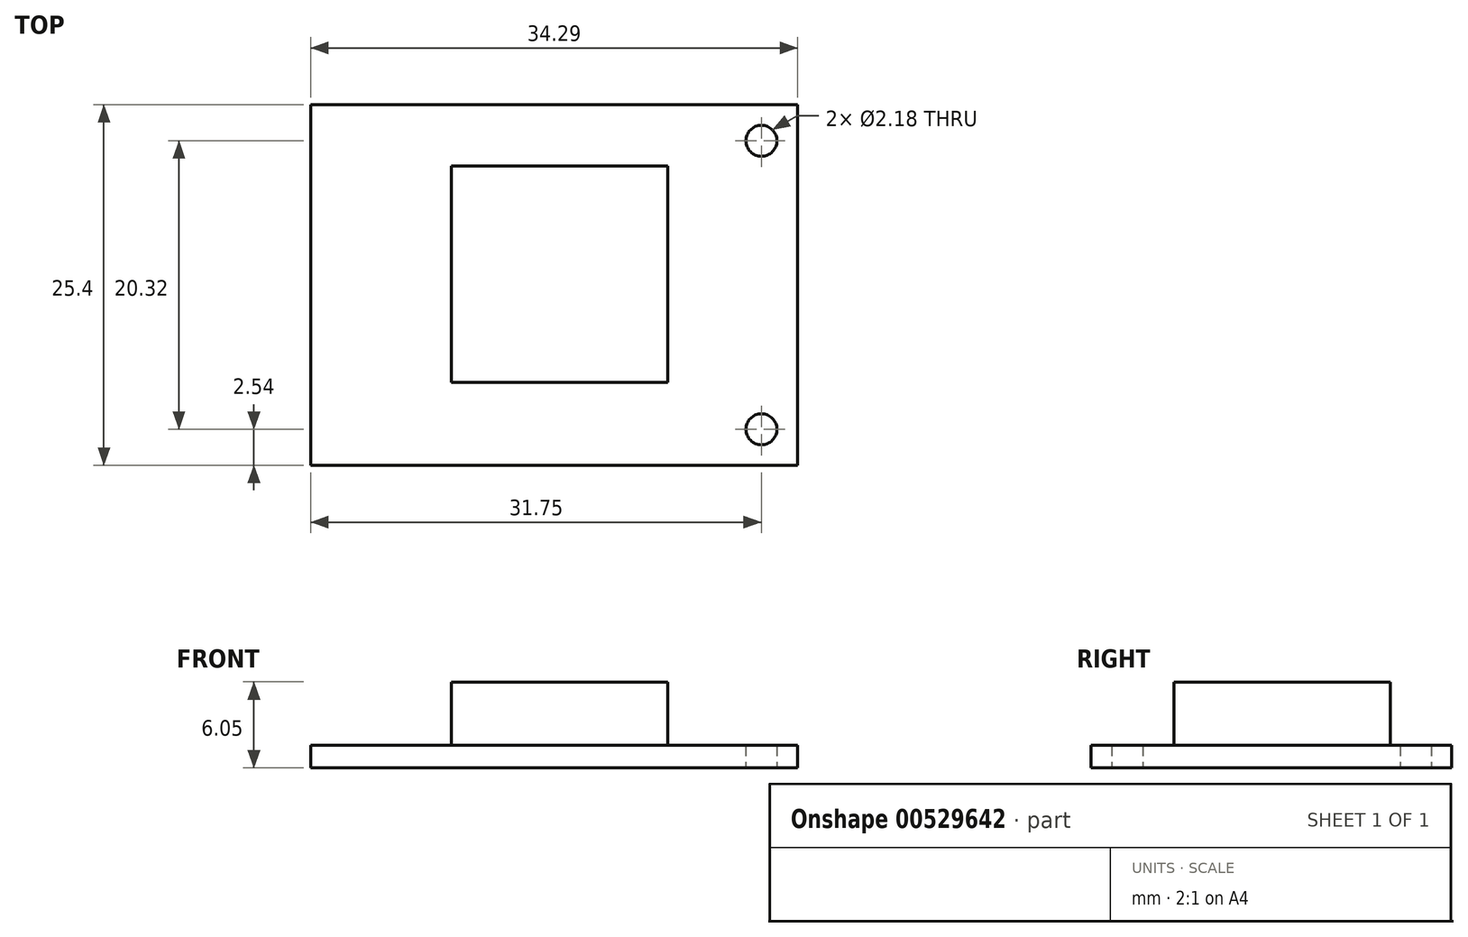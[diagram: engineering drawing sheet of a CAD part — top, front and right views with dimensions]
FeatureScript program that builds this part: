
annotation { "Feature Type Name" : "Feature", "Feature Type Description" : "" }
export const myFeature = defineFeature(function(context is Context, id is Id, definition is map)
    precondition{}
    {
        {
            var Q0;
            Q0=qCreatedBy(makeId("Top.planeOp"),FACE);
            var sketch = newSketch(context, id + "F0", { "sketchPlane" : qUnion([Q0])});
            skLineSegment(sketch, "E0.bottom", {"start": v(0, 0) * mm, "end": v(34.3, 0) * mm});
            skLineSegment(sketch, "E0.top", {"start": v(0, 25.4) * mm, "end": v(34.3, 25.4) * mm});
            skLineSegment(sketch, "E0.left", {"start": v(0, 0) * mm, "end": v(0, 25.4) * mm});
            skLineSegment(sketch, "E0.right", {"start": v(34.3, 0) * mm, "end": v(34.3, 25.4) * mm});
            skCircle(sketch, "E1", {"center": v(31.75, 22.86) * mm, "radius": 1.1 * mm});
            skCircle(sketch, "E2", {"center": v(31.75, 2.54) * mm, "radius": 1.1 * mm});
            skLineSegment(sketch, "E3.bottom", {"start": v(9.9, 21.08) * mm, "end": v(25.15, 21.08) * mm});
            skLineSegment(sketch, "E3.top", {"start": v(9.9, 5.84) * mm, "end": v(25.15, 5.84) * mm});
            skLineSegment(sketch, "E3.left", {"start": v(9.9, 21.08) * mm, "end": v(9.9, 5.84) * mm});
            skLineSegment(sketch, "E3.right", {"start": v(25.15, 21.08) * mm, "end": v(25.15, 5.84) * mm});
            skSolve(sketch);
        }
        {
            var Q0;
            Q0=makeQuery(id+"F0.imprint","IMPRINT",FACE,{"disambiguationData":[TD([[makeQuery(id+"F0.imprint","IMPRINT",EDGE,{"derivedFrom":sQuery(id+"F0.wireOp",EDGE,"E3.bottom")}),-1.0]])]});
            extrude(context, id + "F1", {"entities" : qUnion([Q0]), "depth" : 6.05 * mm, "offsetDistance" : 25.4 * mm});
        }
        {
            var Q0;
            Q0=makeQuery(id+"F0.imprint","IMPRINT",FACE,{"disambiguationData":[TD([[makeQuery(id+"F0.imprint","IMPRINT",EDGE,{"derivedFrom":sQuery(id+"F0.wireOp",EDGE,"E0.bottom")}),1.0]])]});
            extrude(context, id + "F2", {"entities" : qUnion([Q0]), "operationType" : NewBodyOperationType.ADD, "depth" : 1.57 * mm, "offsetDistance" : 25.4 * mm});
        }
    });
